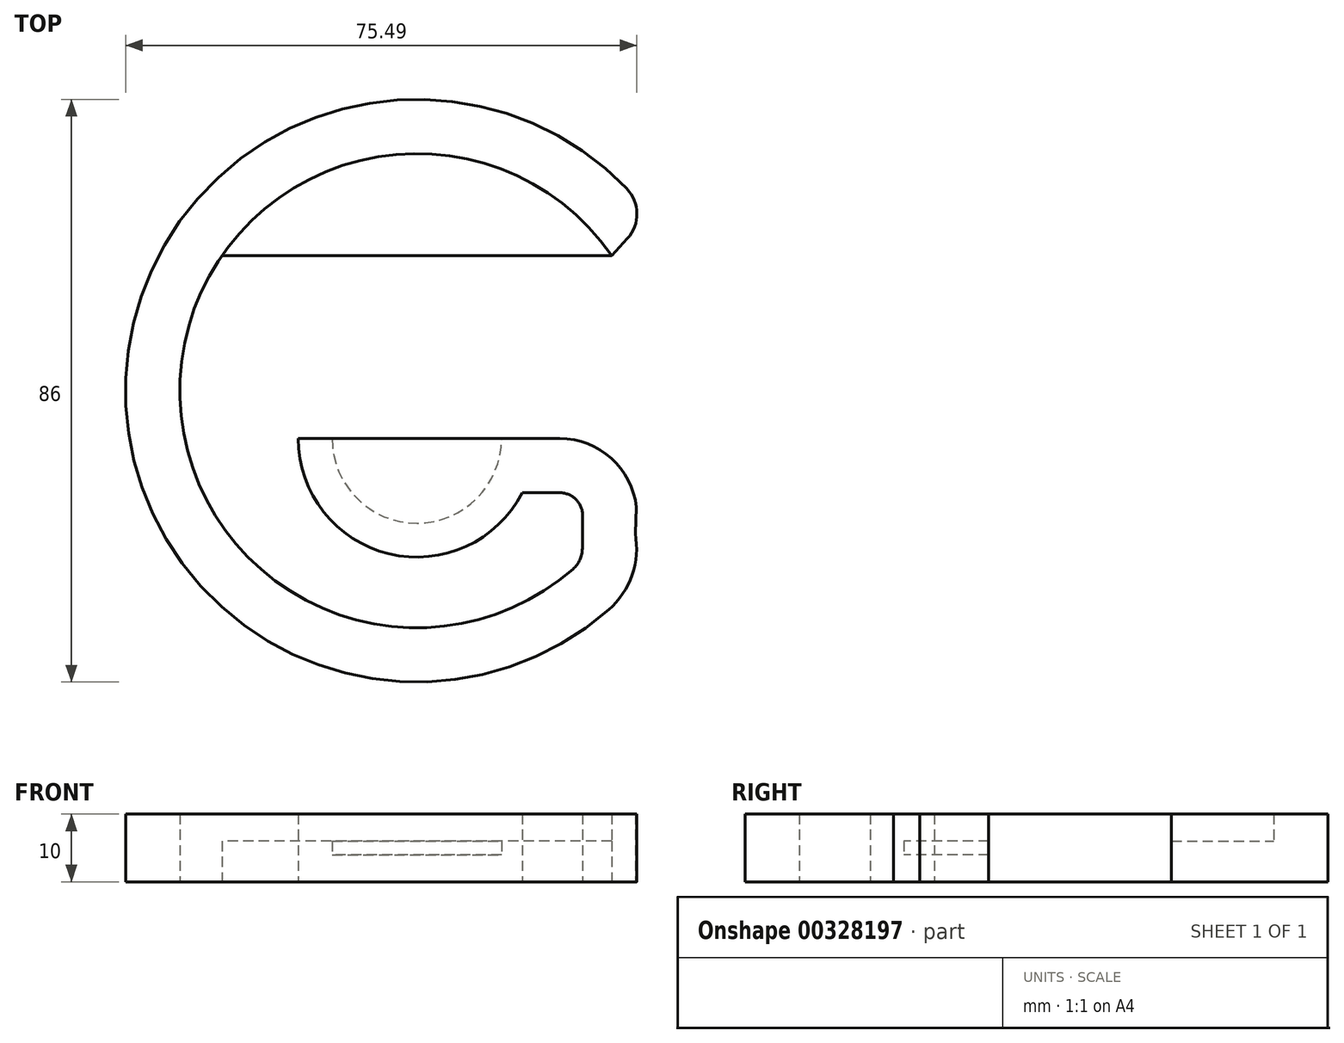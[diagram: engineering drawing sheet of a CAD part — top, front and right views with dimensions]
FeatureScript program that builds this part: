
annotation { "Feature Type Name" : "Feature", "Feature Type Description" : "" }
export const myFeature = defineFeature(function(context is Context, id is Id, definition is map)
    precondition{}
    {
        {
            var Q0;
            Q0=qCreatedBy(makeId("Top.planeOp"),FACE);
            var sketch = newSketch(context, id + "F0", { "sketchPlane" : qUnion([Q0])});
            skArc(sketch, "E0", {"start": v(28.77, 19.93) * mm, "mid": v(-34.74, 4.3) * mm, "end": v(23.05, -26.34) * mm});
            skArc(sketch, "E1.0", {"start": v(30.99, 29.81) * mm, "mid": v(-42.96, 1.85) * mm, "end": v(28.32, -32.36) * mm});
            skLineSegment(sketch, "E2", {"start": v(28.77, 19.93) * mm, "end": v(31.09, 22.47) * mm});
            skLineSegment(sketch, "E3", {"start": v(21.11, -15.07) * mm, "end": v(15.56, -15.07) * mm});
            skLineSegment(sketch, "E4.0", {"start": v(21.11, -7.07) * mm, "end": v(-17.5, -7.07) * mm});
            skLineSegment(sketch, "E5", {"start": v(28.77, 19.93) * mm, "end": v(-28.77, 19.93) * mm});
            skLineSegment(sketch, "E6", {"start": v(32.4, -17.23) * mm, "end": v(32.24, -21.1) * mm, "construction": true});
            skLineSegment(sketch, "E7", {"start": v(32.24, -21.1) * mm, "end": v(32.4, -17.23) * mm});
            skLineSegment(sketch, "E8.trimOffspring", {"start": v(24.47, -18.45) * mm, "end": v(24.44, -23.3) * mm});
            skPoint(sketch, "E9.orphan", {"position": v(31.59, -36.14) * mm});
            skPoint(sketch, "E10.orphan", {"position": v(31.59, -15.07) * mm});
            skPoint(sketch, "E11.visualSharp", {"position": v(24.5, -15.07) * mm});
            skArc(sketch, "E11.filletArc", {"start": v(24.47, -18.45) * mm, "mid": v(23.5, -16.06) * mm, "end": v(21.11, -15.07) * mm});
            skPoint(sketch, "E12.visualSharp", {"position": v(32.85, -7.07) * mm});
            skArc(sketch, "E13.0", {"start": v(32.4, -17.23) * mm, "mid": v(28.7, -9.98) * mm, "end": v(21.11, -7.07) * mm});
            skPoint(sketch, "E14.visualSharp", {"position": v(24.43, -25.07) * mm});
            skArc(sketch, "E14.filletArc", {"start": v(23.05, -26.34) * mm, "mid": v(24.07, -24.97) * mm, "end": v(24.44, -23.3) * mm});
            skArc(sketch, "E15.0", {"start": v(28.32, -32.36) * mm, "mid": v(31.77, -27.24) * mm, "end": v(32.24, -21.1) * mm});
            skArc(sketch, "E16", {"start": v(-12.5, -7.07) * mm, "mid": v(0, -19.57) * mm, "end": v(12.5, -7.07) * mm});
            skPoint(sketch, "E17.visualSharp", {"position": v(34.28, 25.96) * mm});
            skArc(sketch, "E17.filletArc", {"start": v(31.09, 22.47) * mm, "mid": v(32.49, 26.16) * mm, "end": v(30.99, 29.81) * mm});
            skArc(sketch, "E18.0", {"start": v(-17.5, -7.07) * mm, "mid": v(-4.12, -24.08) * mm, "end": v(15.56, -15.07) * mm});
            skSolve(sketch);
        }
        {
            var Q0;
            Q0=makeQuery(id+"F0.imprint","IMPRINT",FACE,{"disambiguationData":[TD([[makeQuery(id+"F0.imprint","IMPRINT",EDGE,{"derivedFrom":sQuery(id+"F0.wireOp",EDGE,"E1.0")}),1.0]])]});
            extrude(context, id + "F1", {"entities" : qUnion([Q0]), "depth" : 10 * mm});
        }
        {
            var Q0;
            {var subQ0=sQuery(id+"F0.wireOp",EDGE,"E5");Q0=makeQuery(id+"F0.imprint","IMPRINT",FACE,{"disambiguationData":[TD([[makeQuery(id+"F0.imprint","IMPRINT",EDGE,{"derivedFrom":subQ0}),-1.0]])]});}
            extrude(context, id + "F2", {"entities" : qUnion([Q0]), "operationType" : NewBodyOperationType.ADD, "depth" : 6 * mm});
        }
        {
            var Q0;
            {var subQ0=sQuery(id+"F0.wireOp",EDGE,"E16");Q0=makeQuery(id+"F0.imprint","IMPRINT",FACE,{"disambiguationData":[TD([[makeQuery(id+"F0.imprint","IMPRINT",EDGE,{"derivedFrom":subQ0}),1.0]])]});}
            extrude(context, id + "F3", {"entities" : qUnion([Q0]), "operationType" : NewBodyOperationType.ADD, "depth" : 10 * mm});
        }
        {
            var Q0;
            {var subQ0=sQuery(id+"F0.wireOp",EDGE,"E16");Q0=makeQuery(id+"F0.imprint","IMPRINT",FACE,{"disambiguationData":[TD([[makeQuery(id+"F0.imprint","IMPRINT",EDGE,{"derivedFrom":subQ0}),1.0]])]});}
            extrude(context, id + "F4", {"entities" : qUnion([Q0]), "operationType" : NewBodyOperationType.REMOVE, "depth" : 6 * mm, "hasSecondDirection" : true, "secondDirectionOppositeDirection" : false, "secondDirectionDepth" : 4 * mm});
        }
    });
